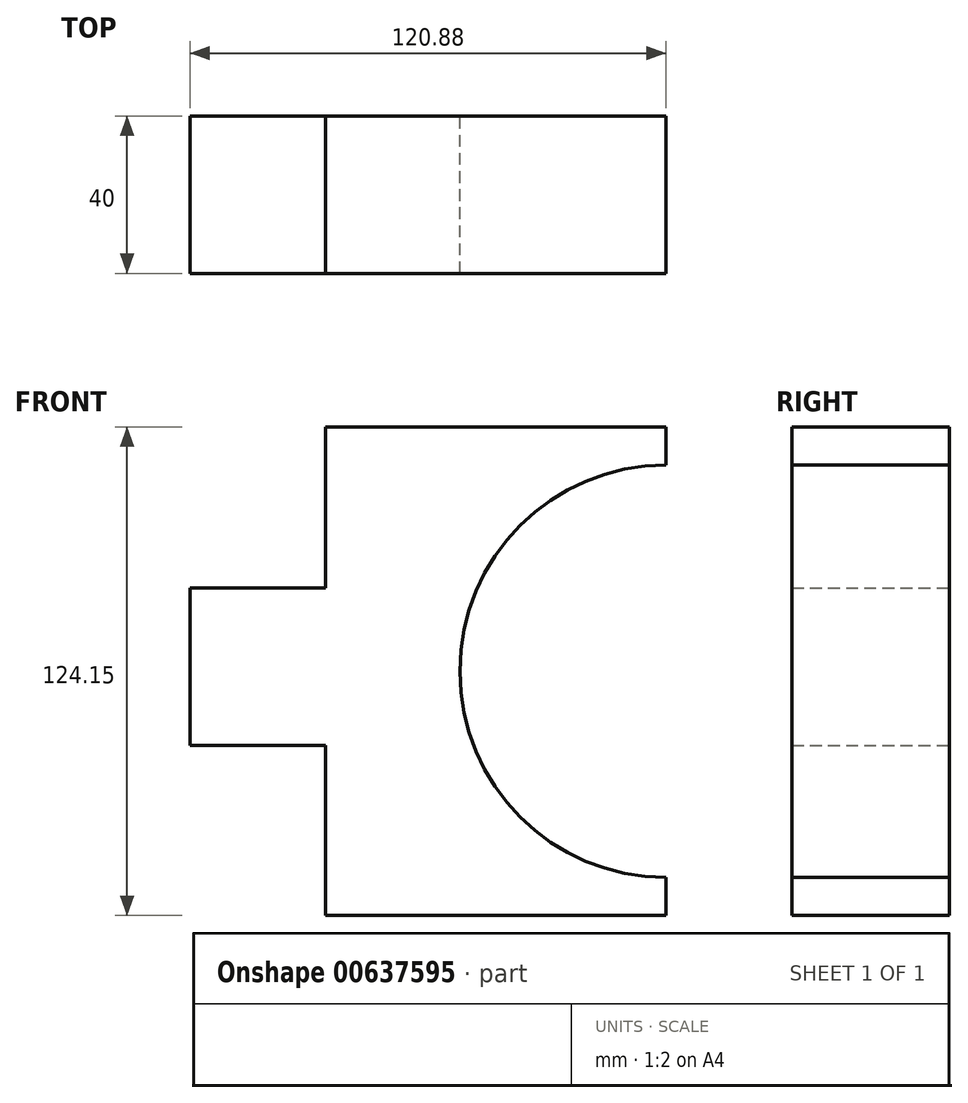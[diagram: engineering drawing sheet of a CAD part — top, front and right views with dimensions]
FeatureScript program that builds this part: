
annotation { "Feature Type Name" : "Feature", "Feature Type Description" : "" }
export const myFeature = defineFeature(function(context is Context, id is Id, definition is map)
    precondition{}
    {
        {
            var Q0;
            Q0=qCreatedBy(makeId("Front.planeOp"),FACE);
            var sketch = newSketch(context, id + "F0", { "sketchPlane" : qUnion([Q0])});
            skLineSegment(sketch, "E0.bottom", {"start": v(-35.56, 53.58) * mm, "end": v(50.95, 53.58) * mm});
            skLineSegment(sketch, "E0.top", {"start": v(-35.56, -70.57) * mm, "end": v(50.95, -70.57) * mm});
            skLineSegment(sketch, "E0.left", {"start": v(-35.56, 53.58) * mm, "end": v(-35.56, 12.69) * mm});
            skLineSegment(sketch, "E0.right", {"start": v(50.95, 53.58) * mm, "end": v(50.95, 43.88) * mm});
            skArc(sketch, "E1", {"start": v(50.95, 43.88) * mm, "mid": v(-1.43, -8.5) * mm, "end": v(50.95, -60.88) * mm});
            skLineSegment(sketch, "E2.trimOffspring", {"start": v(50.95, -60.88) * mm, "end": v(50.95, -70.57) * mm});
            skPoint(sketch, "E3.firstSnap0", {"position": v(-35.56, -8.5) * mm});
            skLineSegment(sketch, "E3.top", {"start": v(-69.93, 12.69) * mm, "end": v(-35.56, 12.69) * mm});
            skLineSegment(sketch, "E3.left", {"start": v(-69.93, -8.5) * mm, "end": v(-69.93, 12.69) * mm});
            skLineSegment(sketch, "E4.top", {"start": v(-69.93, -27.31) * mm, "end": v(-35.56, -27.31) * mm});
            skLineSegment(sketch, "E4.left", {"start": v(-69.93, -8.5) * mm, "end": v(-69.93, -27.31) * mm});
            skLineSegment(sketch, "E5.trimOffspring", {"start": v(-35.56, -27.31) * mm, "end": v(-35.56, -32.94) * mm});
            skLineSegment(sketch, "E6.trimOffspring", {"start": v(-35.56, -27.31) * mm, "end": v(-35.56, -70.57) * mm});
            skSolve(sketch);
        }
        {
            var Q0;
            Q0 = qSketchRegion(id + "F0", true);
            extrude(context, id + "F1", {"entities" : qUnion([Q0]), "depth" : 40 * mm, "offsetDistance" : 25 * mm});
        }
    });
